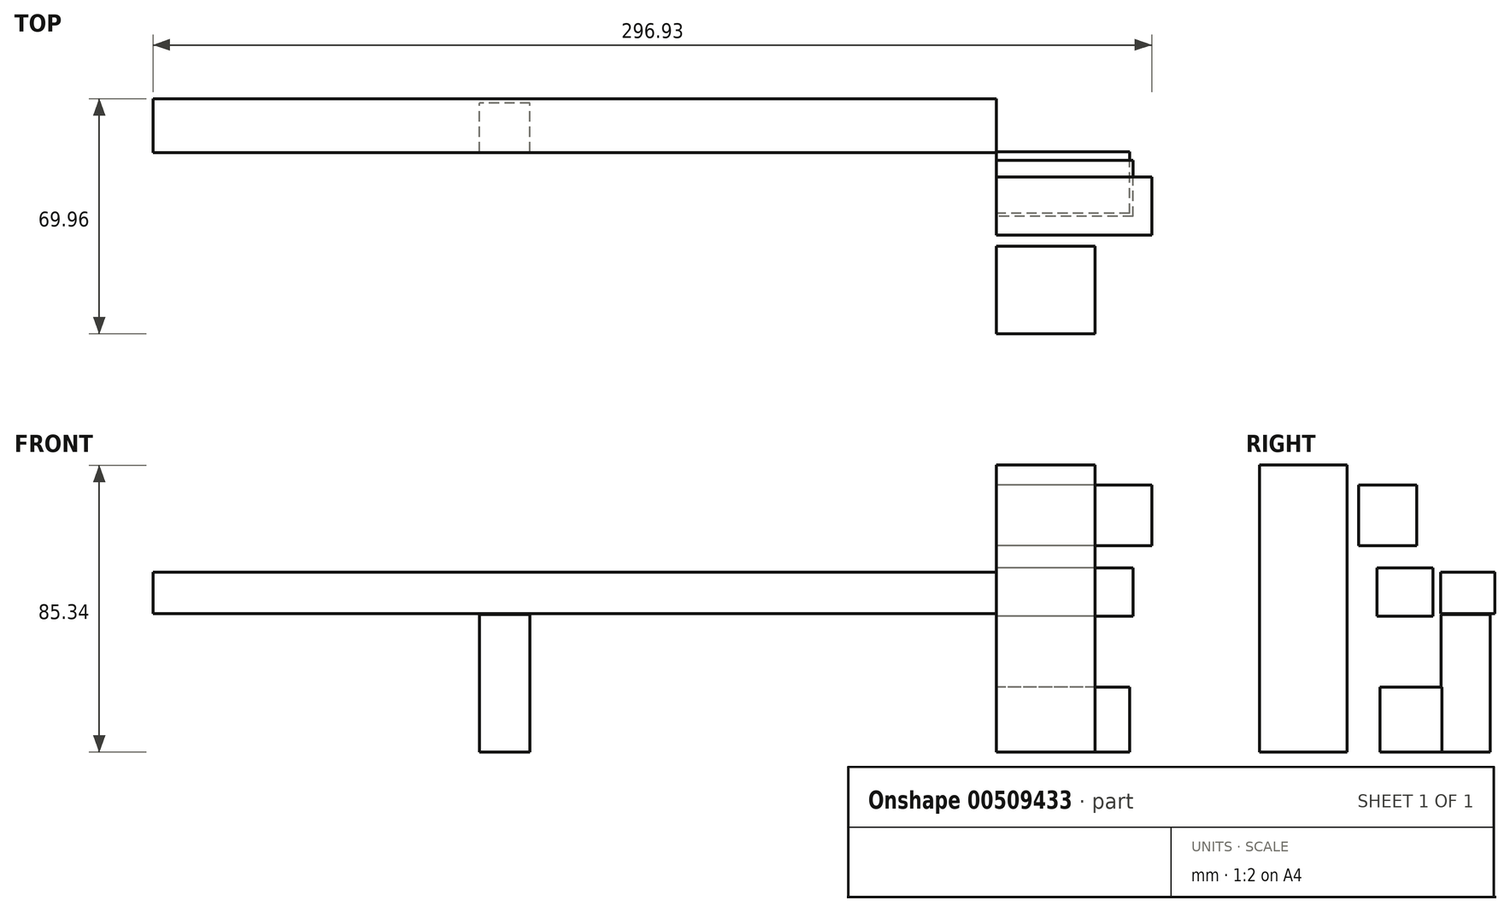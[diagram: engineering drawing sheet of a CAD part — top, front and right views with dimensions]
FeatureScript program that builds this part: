
annotation { "Feature Type Name" : "Feature", "Feature Type Description" : "" }
export const myFeature = defineFeature(function(context is Context, id is Id, definition is map)
    precondition{}
    {
        {
            var Q0;
            Q0=qCreatedBy(makeId("Top.planeOp"),FACE);
            var sketch = newSketch(context, id + "F0", { "sketchPlane" : qUnion([Q0])});
            skLineSegment(sketch, "E0.bottom", {"start": v(-138.61, 7.34) * mm, "end": v(-153.7, 7.34) * mm});
            skLineSegment(sketch, "E0.top", {"start": v(-138.61, 21.93) * mm, "end": v(-153.7, 21.93) * mm});
            skLineSegment(sketch, "E0.left", {"start": v(-138.61, 7.34) * mm, "end": v(-138.61, 21.93) * mm});
            skLineSegment(sketch, "E0.right", {"start": v(-153.7, 7.34) * mm, "end": v(-153.7, 21.93) * mm});
            skPoint(sketch, "E0.middle", {"position": v(-146.15, 14.63) * mm});
            skSolve(sketch);
        }
        {
            var Q0;
            Q0 = qSketchRegion(id + "F0", true);
            extrude(context, id + "F1", {"entities" : qUnion([Q0]), "depth" : 40.9 * mm});
        }
        {
            var Q0;
            Q0=qCreatedBy(makeId("Right.planeOp"),FACE);
            var sketch = newSketch(context, id + "F2", { "sketchPlane" : qUnion([Q0])});
            skLineSegment(sketch, "E1.bottom", {"start": v(7.21, 53.5) * mm, "end": v(23.26, 53.5) * mm});
            skLineSegment(sketch, "E1.top", {"start": v(7.21, 41.17) * mm, "end": v(23.26, 41.17) * mm});
            skLineSegment(sketch, "E1.left", {"start": v(7.21, 53.5) * mm, "end": v(7.21, 41.17) * mm});
            skLineSegment(sketch, "E1.right", {"start": v(23.26, 53.5) * mm, "end": v(23.26, 41.17) * mm});
            skSolve(sketch);
        }
        {
            var Q0;
            Q0 = qSketchRegion(id + "F2", true);
            extrude(context, id + "F3", {"entities" : qUnion([Q0]), "oppositeDirection" : true, "depth" : 250.7 * mm});
        }
        {
            var Q0;
            Q0=qCreatedBy(makeId("Top.planeOp"),FACE);
            var sketch = newSketch(context, id + "F4", { "sketchPlane" : qUnion([Q0])});
            skLineSegment(sketch, "E2.bottom", {"start": v(0, -20.58) * mm, "end": v(29.4, -20.58) * mm});
            skLineSegment(sketch, "E2.top", {"start": v(0, -46.7) * mm, "end": v(29.4, -46.7) * mm});
            skLineSegment(sketch, "E2.left", {"start": v(0, -20.58) * mm, "end": v(0, -46.7) * mm});
            skLineSegment(sketch, "E2.right", {"start": v(29.4, -20.58) * mm, "end": v(29.4, -46.7) * mm});
            skSolve(sketch);
        }
        {
            var Q0;
            Q0 = qSketchRegion(id + "F4", true);
            extrude(context, id + "F5", {"entities" : qUnion([Q0]), "depth" : 85.34 * mm});
        }
        {
            var Q0;
            Q0=qCreatedBy(makeId("Right.planeOp"),FACE);
            var sketch = newSketch(context, id + "F6", { "sketchPlane" : qUnion([Q0])});
            skLineSegment(sketch, "E3.bottom", {"start": v(-11.75, 54.8) * mm, "end": v(4.88, 54.8) * mm});
            skLineSegment(sketch, "E3.top", {"start": v(-11.75, 40.5) * mm, "end": v(4.88, 40.5) * mm});
            skLineSegment(sketch, "E3.left", {"start": v(-11.75, 54.8) * mm, "end": v(-11.75, 40.5) * mm});
            skLineSegment(sketch, "E3.right", {"start": v(4.88, 54.8) * mm, "end": v(4.88, 40.5) * mm});
            skSolve(sketch);
        }
        {
            var Q0;
            Q0 = qSketchRegion(id + "F6", true);
            extrude(context, id + "F7", {"entities" : qUnion([Q0]), "depth" : 40.64 * mm});
        }
        {
            var Q0;
            Q0=qCreatedBy(makeId("Right.planeOp"),FACE);
            var sketch = newSketch(context, id + "F8", { "sketchPlane" : qUnion([Q0])});
            skLineSegment(sketch, "E4.bottom", {"start": v(-17.26, 79.48) * mm, "end": v(0, 79.48) * mm});
            skLineSegment(sketch, "E4.top", {"start": v(-17.26, 61.46) * mm, "end": v(0, 61.46) * mm});
            skLineSegment(sketch, "E4.left", {"start": v(-17.26, 79.48) * mm, "end": v(-17.26, 61.46) * mm});
            skLineSegment(sketch, "E4.right", {"start": v(0, 79.48) * mm, "end": v(0, 61.46) * mm});
            skSolve(sketch);
        }
        {
            var Q0;
            Q0 = qSketchRegion(id + "F8", true);
            extrude(context, id + "F9", {"entities" : qUnion([Q0]), "depth" : 46.23 * mm});
        }
        {
            var Q0;
            Q0=qCreatedBy(makeId("Right.planeOp"),FACE);
            var sketch = newSketch(context, id + "F10", { "sketchPlane" : qUnion([Q0])});
            skLineSegment(sketch, "E5.bottom", {"start": v(-10.9, 19.35) * mm, "end": v(7.49, 19.35) * mm});
            skLineSegment(sketch, "E5.top", {"start": v(-10.9, 0) * mm, "end": v(7.49, 0) * mm});
            skLineSegment(sketch, "E5.left", {"start": v(-10.9, 19.35) * mm, "end": v(-10.9, 0) * mm});
            skLineSegment(sketch, "E5.right", {"start": v(7.49, 19.35) * mm, "end": v(7.49, 0) * mm});
            skSolve(sketch);
        }
        {
            var Q0;
            Q0 = qSketchRegion(id + "F10", true);
            extrude(context, id + "F11", {"entities" : qUnion([Q0]), "depth" : 39.62 * mm});
        }
    });
